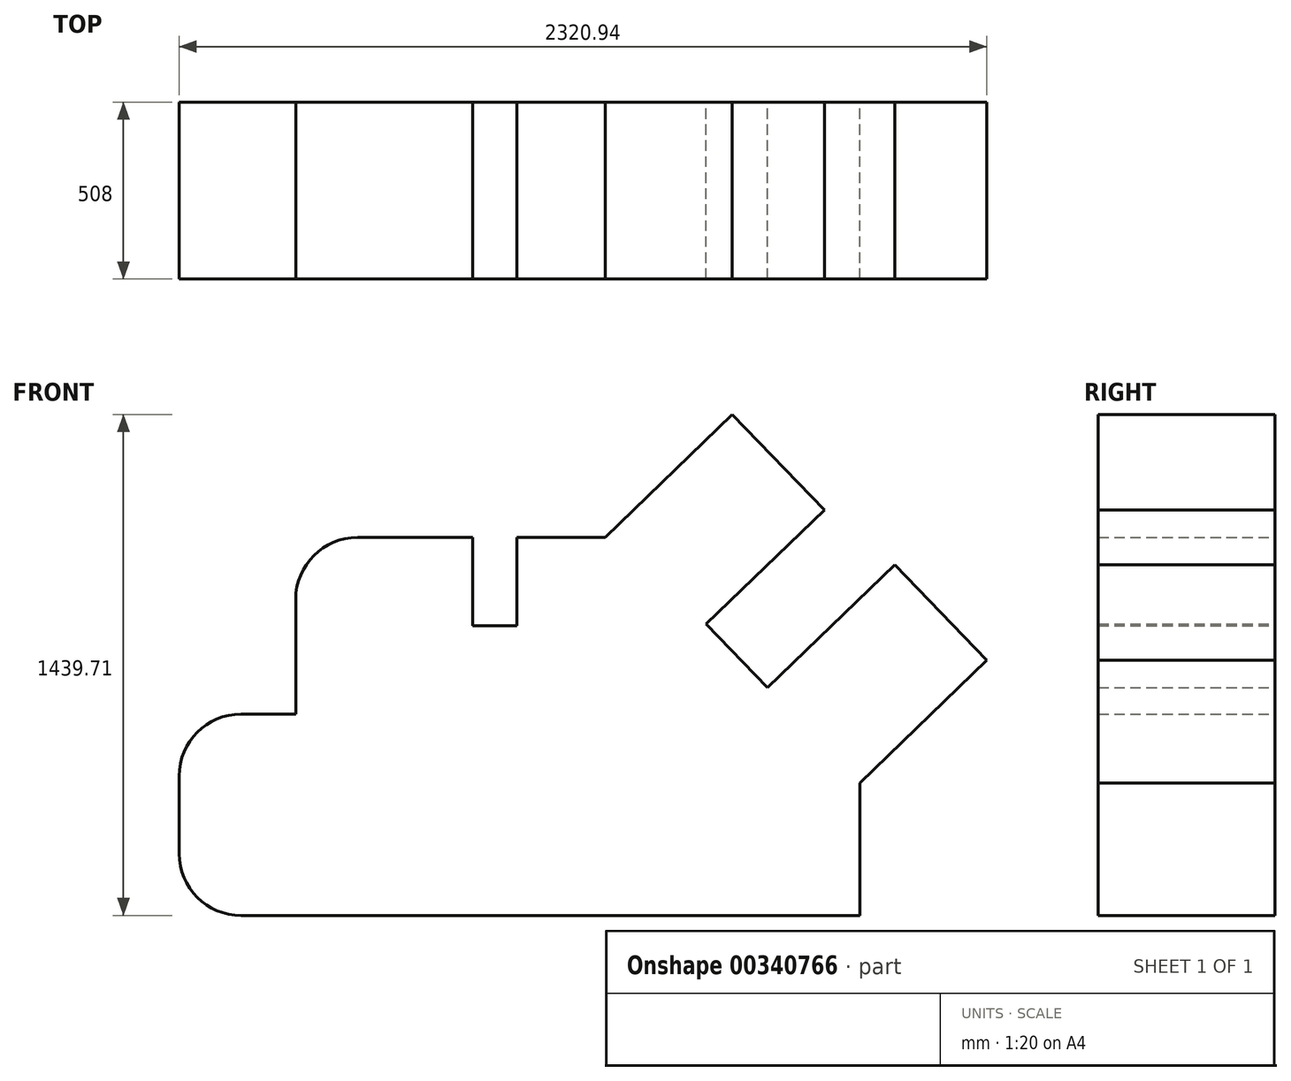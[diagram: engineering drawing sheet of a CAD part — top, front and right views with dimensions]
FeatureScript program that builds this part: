
annotation { "Feature Type Name" : "Feature", "Feature Type Description" : "" }
export const myFeature = defineFeature(function(context is Context, id is Id, definition is map)
    precondition{}
    {
        {
            var Q0;
            Q0=qCreatedBy(makeId("Front.planeOp"),FACE);
            var sketch = newSketch(context, id + "F0", { "sketchPlane" : qUnion([Q0])});
            skLineSegment(sketch, "E0", {"start": v(-940.24, -30.32) * mm, "end": v(-940.24, 192.6) * mm});
            skLineSegment(sketch, "E1", {"start": v(-762.44, 370.4) * mm, "end": v(-605.39, 370.4) * mm});
            skLineSegment(sketch, "E2", {"start": v(-605.39, 370.4) * mm, "end": v(-605.39, 700.6) * mm});
            skPoint(sketch, "E3.visualSharp", {"position": v(-940.24, 370.4) * mm});
            skArc(sketch, "E3.filletArc", {"start": v(-762.44, 370.4) * mm, "mid": v(-888.16, 318.33) * mm, "end": v(-940.24, 192.6) * mm});
            skPoint(sketch, "E4.visualSharp", {"position": v(-940.24, -137.6) * mm});
            skArc(sketch, "E4.filletArc", {"start": v(-940.24, -30.32) * mm, "mid": v(-888.16, -156.04) * mm, "end": v(-762.44, -208.12) * mm});
            skLineSegment(sketch, "E5", {"start": v(-427.59, 878.4) * mm, "end": v(-97.39, 878.4) * mm});
            skPoint(sketch, "E6.visualSharp", {"position": v(-605.39, 878.4) * mm});
            skArc(sketch, "E6.filletArc", {"start": v(-427.59, 878.4) * mm, "mid": v(-553.3, 826.33) * mm, "end": v(-605.39, 700.6) * mm});
            skLineSegment(sketch, "E7", {"start": v(-97.39, 878.4) * mm, "end": v(-97.39, 624.4) * mm});
            skLineSegment(sketch, "E8", {"start": v(-97.39, 624.4) * mm, "end": v(29.61, 624.4) * mm});
            skLineSegment(sketch, "E9", {"start": v(29.61, 624.4) * mm, "end": v(29.61, 878.4) * mm});
            skLineSegment(sketch, "E10", {"start": v(29.61, 878.4) * mm, "end": v(283.61, 878.4) * mm});
            skLineSegment(sketch, "E11", {"start": v(-762.44, -208.12) * mm, "end": v(1015.56, -208.12) * mm});
            skLineSegment(sketch, "E12", {"start": v(1015.56, -208.12) * mm, "end": v(1015.56, 172.88) * mm});
            skLineSegment(sketch, "E13", {"start": v(1015.56, 172.88) * mm, "end": v(1380.7, 526.06) * mm});
            skLineSegment(sketch, "E14", {"start": v(1380.7, 526.06) * mm, "end": v(1115.82, 799.91) * mm});
            skLineSegment(sketch, "E15", {"start": v(1115.82, 799.91) * mm, "end": v(750.68, 446.73) * mm});
            skLineSegment(sketch, "E16", {"start": v(750.68, 446.73) * mm, "end": v(574.09, 629.3) * mm});
            skLineSegment(sketch, "E17", {"start": v(574.09, 629.3) * mm, "end": v(939.23, 982.48) * mm});
            skLineSegment(sketch, "E18", {"start": v(283.61, 878.4) * mm, "end": v(648.75, 1231.6) * mm});
            skLineSegment(sketch, "E19", {"start": v(648.75, 1231.6) * mm, "end": v(913.64, 957.74) * mm});
            skSolve(sketch);
        }
        {
            var Q0;
            Q0=makeQuery(id+"F0.imprint","IMPRINT",FACE,{"disambiguationData":[TD([[makeQuery(id+"F0.imprint","IMPRINT",EDGE,{"derivedFrom":sQuery(id+"F0.wireOp",EDGE,"E0")}),-1.0]])]});
            extrude(context, id + "F1", {"entities" : qUnion([Q0]), "depth" : 508 * mm});
        }
    });
